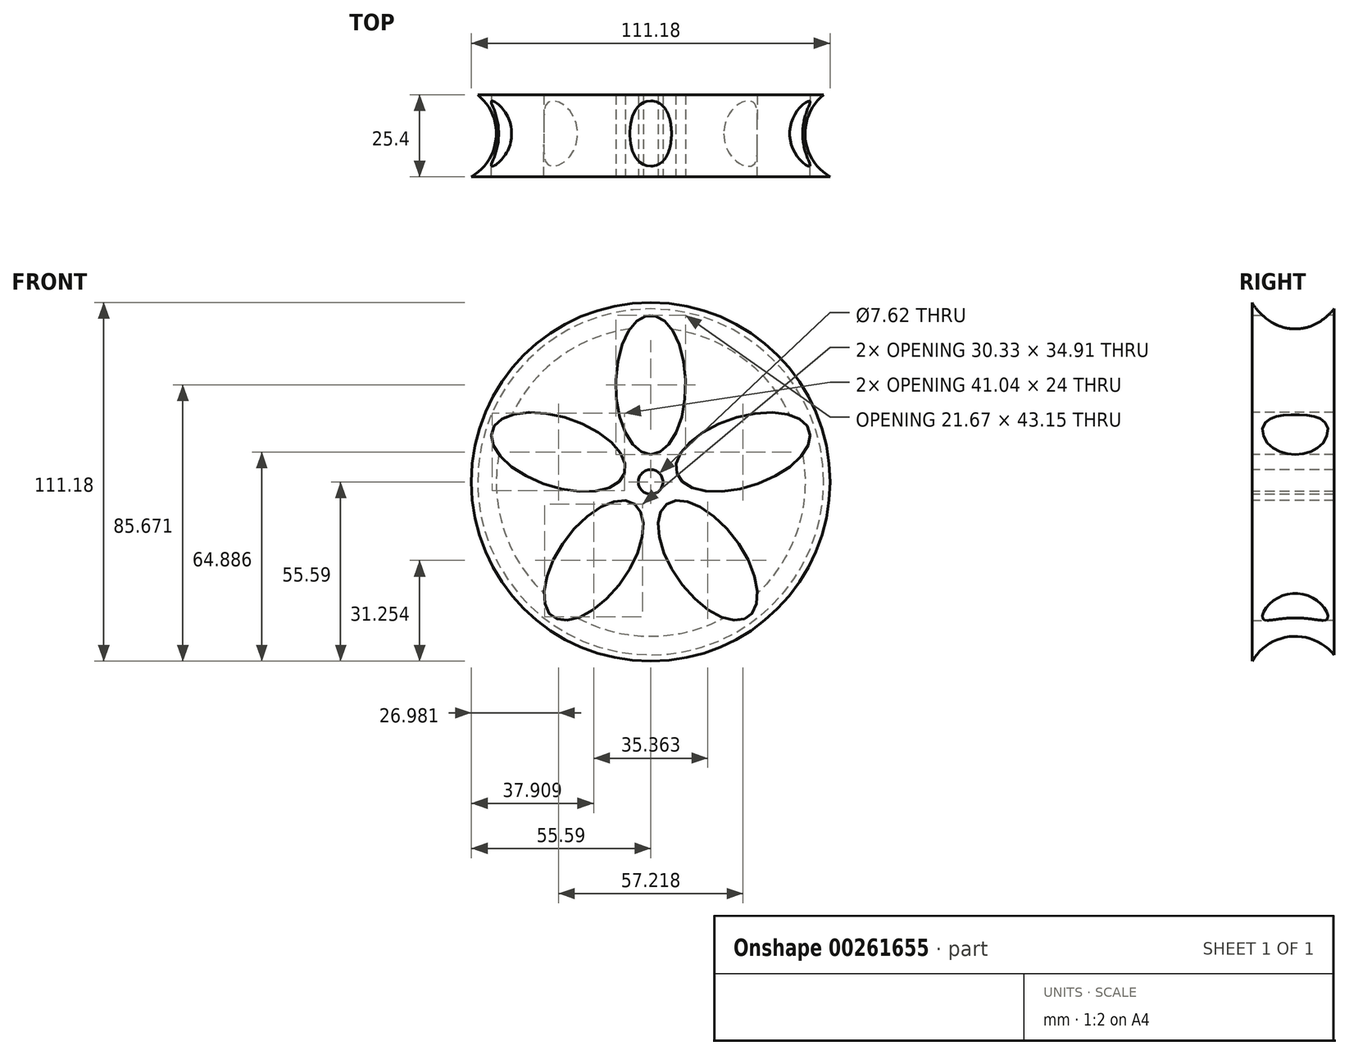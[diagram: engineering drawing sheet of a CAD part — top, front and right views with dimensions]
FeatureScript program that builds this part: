
annotation { "Feature Type Name" : "Feature", "Feature Type Description" : "" }
export const myFeature = defineFeature(function(context is Context, id is Id, definition is map)
    precondition{}
    {
        {
            var Q0;
            Q0=qCreatedBy(makeId("Front.planeOp"),FACE);
            var sketch = newSketch(context, id + "F0", { "sketchPlane" : qUnion([Q0])});
            skCircle(sketch, "E0", {"center": v(0, 0) * mm, "radius": 58.34 * mm});
            skSolve(sketch);
        }
        {
            var Q0;
            Q0=makeQuery(id+"F0.imprint","IMPRINT",FACE,{"disambiguationData":[TD([[makeQuery(id+"F0.imprint","IMPRINT",EDGE,{"derivedFrom":sQuery(id+"F0.wireOp",EDGE,"E0")}),1.0]])]});
            var Q1;
            Q1 = qSketchRegion(id + "F0", true);
            extrude(context, id + "F1", {"entities" : qUnion([Q0, Q1]), "depth" : 25.4 * mm});
        }
        {
            var Q0;
            Q0=makeQuery(id+"F1.opExtrude","CAP_FACE",FACE,{"disambiguationData":[OSD([sQuery(id+"F0.wireOp",EDGE,"E0")])],"isStart":false});
            var sketch = newSketch(context, id + "F2", { "sketchPlane" : qUnion([Q0])});
            skEllipse(sketch, "E1", {"center": v(0, 30.08) * mm, "majorRadius": 21.58 * mm, "minorRadius": 10.83 * mm, "majorAxis": v(0, -1)});
            skEllipse(sketch, "E2.1.0", {"center": v(-28.6, 9.3) * mm, "majorRadius": 21.58 * mm, "minorRadius": 10.83 * mm, "majorAxis": v(0.95, -0.3)});
            skEllipse(sketch, "E2.2.0", {"center": v(-17.68, -24.34) * mm, "majorRadius": 21.58 * mm, "minorRadius": 10.83 * mm, "majorAxis": v(0.59, 0.8)});
            skEllipse(sketch, "E2.3.0", {"center": v(17.68, -24.34) * mm, "majorRadius": 21.58 * mm, "minorRadius": 10.83 * mm, "majorAxis": v(-0.59, 0.8)});
            skEllipse(sketch, "E2.4.0", {"center": v(28.6, 9.3) * mm, "majorRadius": 21.58 * mm, "minorRadius": 10.83 * mm, "majorAxis": v(-0.95, -0.3)});
            skPoint(sketch, "E2.center", {"position": v(0, 0) * mm});
            skSolve(sketch);
        }
        {
            var Q0;
            Q0=makeQuery(id+"F2.imprint","IMPRINT",FACE,{"disambiguationData":[TD([[makeQuery(id+"F2.imprint","IMPRINT",EDGE,{"derivedFrom":sQuery(id+"F2.wireOp",EDGE,"E1")}),1.0]])]});
            var sketch = newSketch(context, id + "F3", { "sketchPlane" : qUnion([Q0])});
            skSolve(sketch);
        }
        {
            var Q0;
            Q0=makeQuery(id+"F2.imprint","IMPRINT",FACE,{"disambiguationData":[TD([[makeQuery(id+"F2.imprint","IMPRINT",EDGE,{"derivedFrom":sQuery(id+"F2.wireOp",EDGE,"E2.3.0")}),1.0]])]});
            var Q1;
            Q1=makeQuery(id+"F2.imprint","IMPRINT",FACE,{"disambiguationData":[TD([[makeQuery(id+"F2.imprint","IMPRINT",EDGE,{"derivedFrom":sQuery(id+"F2.wireOp",EDGE,"E2.1.0")}),1.0]])]});
            var Q2;
            Q2=makeQuery(id+"F2.imprint","IMPRINT",FACE,{"disambiguationData":[TD([[makeQuery(id+"F2.imprint","IMPRINT",EDGE,{"derivedFrom":sQuery(id+"F2.wireOp",EDGE,"E2.2.0")}),1.0]])]});
            var Q3;
            Q3=makeQuery(id+"F2.imprint","IMPRINT",FACE,{"disambiguationData":[TD([[makeQuery(id+"F2.imprint","IMPRINT",EDGE,{"derivedFrom":sQuery(id+"F2.wireOp",EDGE,"E2.4.0")}),1.0]])]});
            var Q4;
            Q4=makeQuery(id+"F3.imprint","IMPRINT",FACE,{"disambiguationData":[TD([[makeQuery(id+"F3.imprint","IMPRINT",EDGE,{"derivedFrom":makeQuery(id+"F2.imprint","IMPRINT",EDGE,{"derivedFrom":sQuery(id+"F2.wireOp",EDGE,"E1")})}),1.0]])]});
            extrude(context, id + "F4", {"entities" : qUnion([Q0, Q1, Q2, Q3, Q4]), "operationType" : NewBodyOperationType.REMOVE, "oppositeDirection" : true, "depth" : 25.4 * mm});
        }
        {
            var Q0;
            Q0=qCreatedBy(makeId("Right.planeOp"),FACE);
            var sketch = newSketch(context, id + "F5", { "sketchPlane" : qUnion([Q0])});
            skCircle(sketch, "E3", {"center": v(-12.03, 63.27) * mm, "radius": 15.42 * mm});
            skSolve(sketch);
        }
        {
            var Q0;
            Q0 = qSketchRegion(id + "F5", true);
            var Q1;
            Q1=makeQuery(id+"F1.opExtrude","CAP_EDGE",EDGE,{"disambiguationData":[OSD([sQuery(id+"F0.wireOp",EDGE,"E0")])],"isStart":false});
            revolve(context, id + "F6", {"operationType" : NewBodyOperationType.REMOVE, "entities" : qUnion([Q0]), "axis" : qUnion([Q1]), "revolveType" : RevolveType.FULL, "oppositeDirection" : true});
        }
        {
            var Q0;
            Q0=makeQuery(id+"F1.opExtrude","CAP_FACE",FACE,{"disambiguationData":[OSD([sQuery(id+"F0.wireOp",EDGE,"E0")])],"isStart":false});
            var sketch = newSketch(context, id + "F7", { "sketchPlane" : qUnion([Q0])});
            skPoint(sketch, "E4", {"position": v(0, 0) * mm});
            skSolve(sketch);
        }
        {
            var Q0;
            Q0=sQuery(id+"F7.wireOp",VERTEX,"E4");
            var Q1;
            Q1=makeQuery(id+"F1.opExtrude","SWEPT_BODY",BODY,{"disambiguationData":[OSD([sQuery(id+"F0.wireOp",EDGE,"E0")])]});
            hole(context, id + "F8", {"style" : HoleStyle.SIMPLE, "endStyle" : HoleEndStyle.THROUGH, "holeDiameter" : 7.62 * mm, "tappedDepth" : 12.7 * mm, "tapClearance" : 3, "locations" : qUnion([Q0]), "scope" : qUnion([Q1])});
        }
    });
